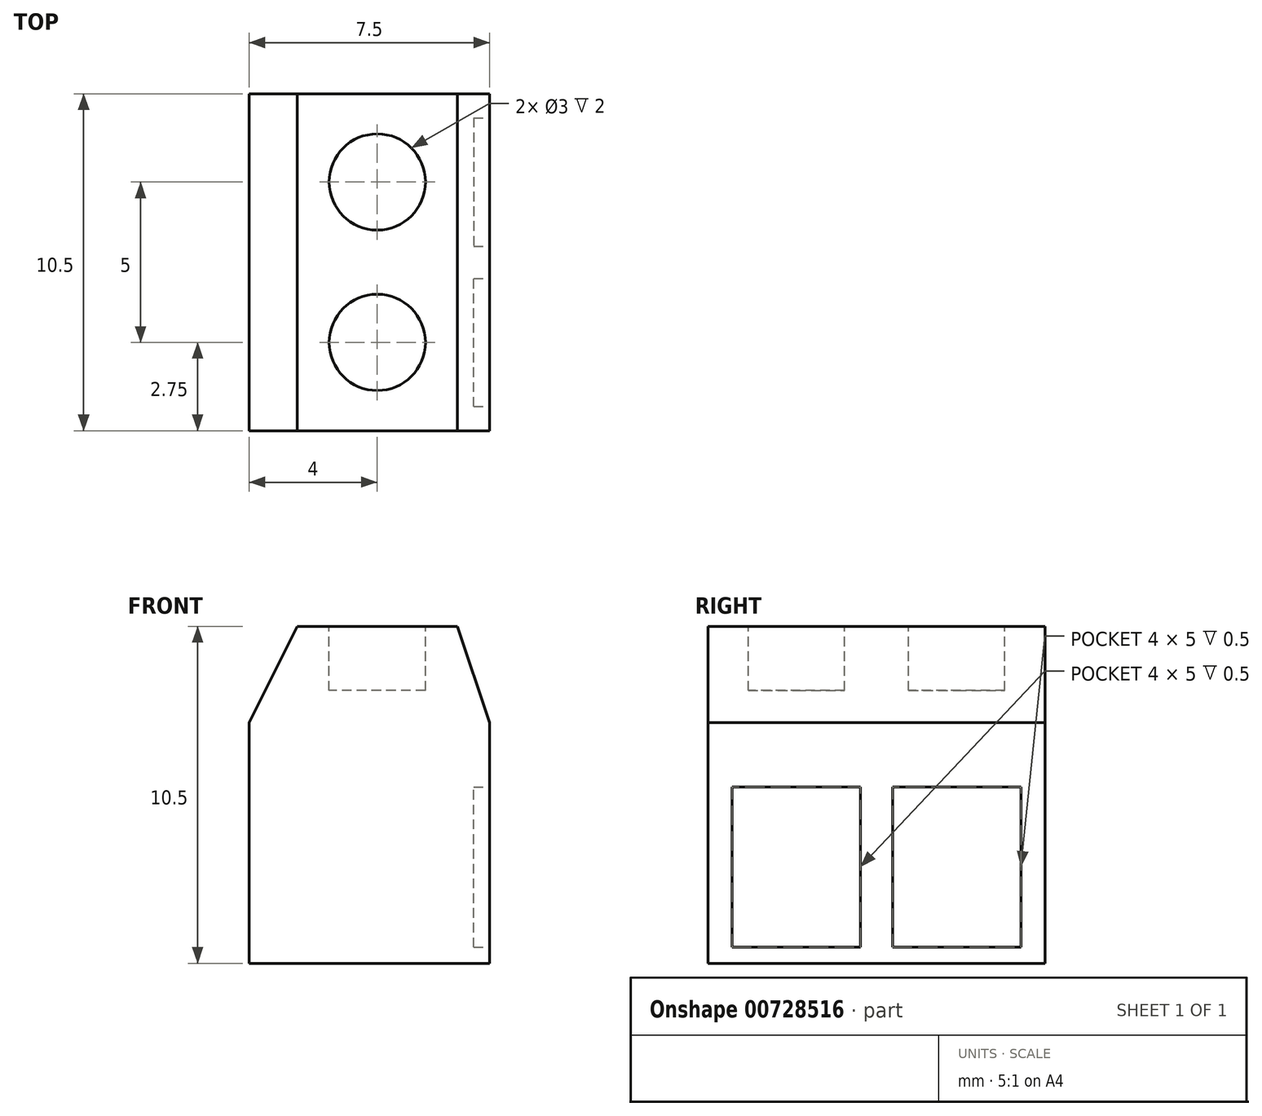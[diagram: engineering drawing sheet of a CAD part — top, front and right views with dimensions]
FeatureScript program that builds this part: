
annotation { "Feature Type Name" : "Feature", "Feature Type Description" : "" }
export const myFeature = defineFeature(function(context is Context, id is Id, definition is map)
    precondition{}
    {
        {
            var Q0;
            Q0=qCreatedBy(makeId("Front.planeOp"),FACE);
            var sketch = newSketch(context, id + "F0", { "sketchPlane" : qUnion([Q0])});
            skLineSegment(sketch, "E0.bottom", {"start": v(0, 0) * mm, "end": v(-7.5, 0) * mm});
            skLineSegment(sketch, "E0.top", {"start": v(0, 10.5) * mm, "end": v(-7.5, 10.5) * mm});
            skLineSegment(sketch, "E0.left", {"start": v(0, 0) * mm, "end": v(0, 10.5) * mm});
            skLineSegment(sketch, "E0.right", {"start": v(-7.5, 0) * mm, "end": v(-7.5, 10.5) * mm});
            skSolve(sketch);
        }
        {
            var Q0;
            Q0 = qSketchRegion(id + "F0", true);
            extrude(context, id + "F1", {"entities" : qUnion([Q0]), "oppositeDirection" : true, "depth" : 10.5 * mm, "offsetDistance" : 25 * mm});
        }
        {
            var Q0;
            Q0=makeQuery(id+"F1.opExtrude","SWEPT_EDGE",EDGE,{"disambiguationData":[OSD([sQuery(id+"F0.wireOp",EDGE,"E0.top"),sQuery(id+"F0.wireOp",EDGE,"E0.right")])]});
            chamfer(context, id + "F2", {"entities" : qUnion([Q0]), "chamferType" : ChamferType.TWO_OFFSETS, "width1" : 1.5 * mm, "oppositeDirection" : false, "width2" : 3 * mm, "tangentPropagation" : true});
        }
        {
            var Q0;
            Q0=makeQuery(id+"F1.opExtrude","SWEPT_EDGE",EDGE,{"disambiguationData":[OSD([sQuery(id+"F0.wireOp",EDGE,"E0.top"),sQuery(id+"F0.wireOp",EDGE,"E0.left")])]});
            chamfer(context, id + "F3", {"entities" : qUnion([Q0]), "chamferType" : ChamferType.TWO_OFFSETS, "width1" : 3 * mm, "oppositeDirection" : false, "width2" : 1 * mm, "tangentPropagation" : true});
        }
        {
            var Q0;
            Q0=makeQuery(id+"F1.opExtrude","SWEPT_FACE",FACE,{"disambiguationData":[OSD([sQuery(id+"F0.wireOp",EDGE,"E0.top")])]});
            var sketch = newSketch(context, id + "F4", { "sketchPlane" : qUnion([Q0])});
            skCircle(sketch, "E1", {"center": v(-3.5, 2.75) * mm, "radius": 1.5 * mm});
            skLineSegment(sketch, "E2", {"start": v(-3.5, 10.5) * mm, "end": v(-3.5, 0) * mm, "construction": true});
            skCircle(sketch, "E3.0.1.0", {"center": v(-3.5, 7.75) * mm, "radius": 1.5 * mm});
            skLineSegment(sketch, "E3.direction2", {"start": v(-3.5, 2.75) * mm, "end": v(-3.5, 7.75) * mm, "construction": true});
            skLineSegment(sketch, "E4", {"start": v(-3.5, 5.25) * mm, "end": v(-5, 5.25) * mm, "construction": true});
            skLineSegment(sketch, "E5", {"start": v(-6, 5.25) * mm, "end": v(-1, 5.25) * mm, "construction": true});
            skSolve(sketch);
        }
        {
            var Q0;
            Q0 = qSketchRegion(id + "F4", true);
            extrude(context, id + "F5", {"entities" : qUnion([Q0]), "operationType" : NewBodyOperationType.REMOVE, "oppositeDirection" : true, "depth" : 2 * mm, "offsetDistance" : 25 * mm});
        }
        {
            var Q0;
            Q0=makeQuery(id+"F1.opExtrude","SWEPT_FACE",FACE,{"disambiguationData":[OSD([sQuery(id+"F0.wireOp",EDGE,"E0.left")])]});
            var sketch = newSketch(context, id + "F6", { "sketchPlane" : qUnion([Q0])});
            skLineSegment(sketch, "E6.bottom", {"start": v(0.75, 0.5) * mm, "end": v(4.75, 0.5) * mm});
            skLineSegment(sketch, "E6.top", {"start": v(0.75, 5.5) * mm, "end": v(4.75, 5.5) * mm});
            skLineSegment(sketch, "E6.left", {"start": v(0.75, 0.5) * mm, "end": v(0.75, 5.5) * mm});
            skLineSegment(sketch, "E6.right", {"start": v(4.75, 0.5) * mm, "end": v(4.75, 5.5) * mm});
            skLineSegment(sketch, "E7", {"start": v(5.25, 0) * mm, "end": v(5.25, 7.5) * mm, "construction": true});
            skLineSegment(sketch, "E8.MirrorCS", {"start": v(9.75, 5.5) * mm, "end": v(5.75, 5.5) * mm});
            skLineSegment(sketch, "E9.MirrorCS", {"start": v(5.75, 0.5) * mm, "end": v(5.75, 5.5) * mm});
            skLineSegment(sketch, "E10.MirrorCS", {"start": v(9.75, 0.5) * mm, "end": v(5.75, 0.5) * mm});
            skLineSegment(sketch, "E11.MirrorCS", {"start": v(9.75, 0.5) * mm, "end": v(9.75, 5.5) * mm});
            skSolve(sketch);
        }
        {
            var Q0;
            Q0=makeQuery(id+"F6.imprint","IMPRINT",FACE,{"disambiguationData":[TD([[makeQuery(id+"F6.imprint","IMPRINT",EDGE,{"derivedFrom":sQuery(id+"F6.wireOp",EDGE,"E6.bottom")}),1.0]])]});
            var Q1;
            Q1=makeQuery(id+"F6.imprint","IMPRINT",FACE,{"disambiguationData":[TD([[makeQuery(id+"F6.imprint","IMPRINT",EDGE,{"derivedFrom":sQuery(id+"F6.wireOp",EDGE,"E8.MirrorCS")}),1.0]])]});
            extrude(context, id + "F7", {"entities" : qUnion([Q0, Q1]), "operationType" : NewBodyOperationType.REMOVE, "oppositeDirection" : true, "depth" : 0.5 * mm, "offsetDistance" : 25 * mm});
        }
    });
